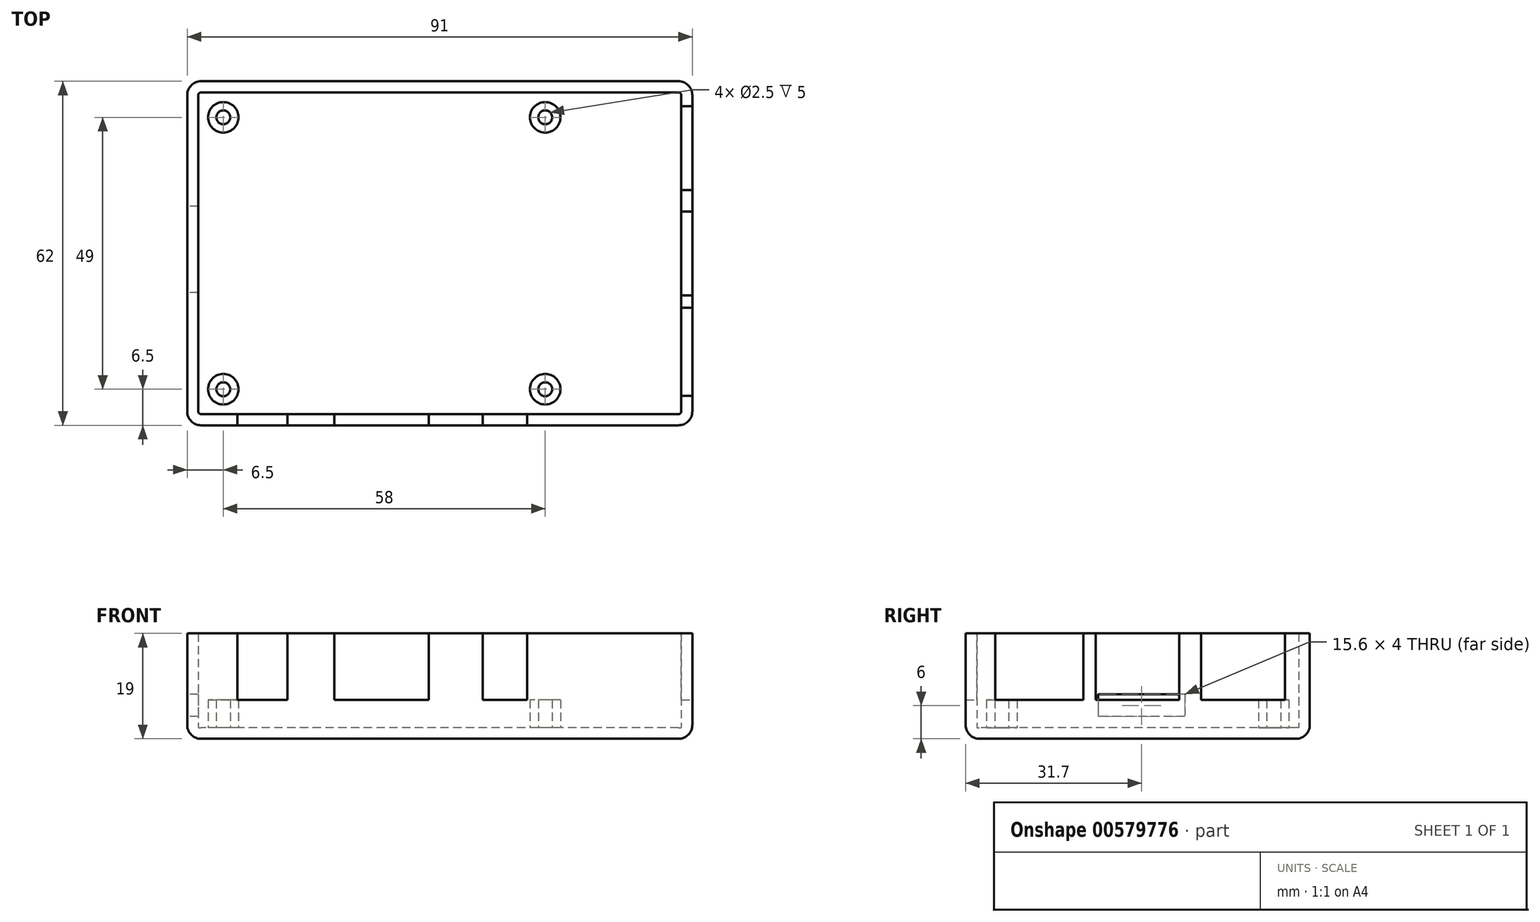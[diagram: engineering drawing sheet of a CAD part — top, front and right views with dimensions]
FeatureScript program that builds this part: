
annotation { "Feature Type Name" : "Feature", "Feature Type Description" : "" }
export const myFeature = defineFeature(function(context is Context, id is Id, definition is map)
    precondition{}
    {
        {
            var Q0;
            Q0=qCreatedBy(makeId("Top.planeOp"),FACE);
            var sketch = newSketch(context, id + "F0", { "sketchPlane" : qUnion([Q0])});
            skLineSegment(sketch, "E0.bottom", {"start": v(2.5, 0) * mm, "end": v(88.5, 0) * mm});
            skLineSegment(sketch, "E0.top", {"start": v(2.5, 62) * mm, "end": v(88.5, 62) * mm});
            skLineSegment(sketch, "E0.left", {"start": v(0, 2.5) * mm, "end": v(0, 59.5) * mm});
            skLineSegment(sketch, "E0.right", {"start": v(91, 2.5) * mm, "end": v(91, 59.5) * mm});
            skPoint(sketch, "E1.visualSharp", {"position": v(91, 62) * mm});
            skArc(sketch, "E1.filletArc", {"start": v(91, 59.5) * mm, "mid": v(90.27, 61.27) * mm, "end": v(88.5, 62) * mm});
            skPoint(sketch, "E2.visualSharp", {"position": v(91, 0) * mm});
            skArc(sketch, "E2.filletArc", {"start": v(88.5, 0) * mm, "mid": v(90.27, 0.73) * mm, "end": v(91, 2.5) * mm});
            skPoint(sketch, "E3.visualSharp", {"position": v(0, 0) * mm});
            skArc(sketch, "E3.filletArc", {"start": v(0, 2.5) * mm, "mid": v(0.73, 0.73) * mm, "end": v(2.5, 0) * mm});
            skPoint(sketch, "E4.visualSharp", {"position": v(0, 62) * mm});
            skArc(sketch, "E4.filletArc", {"start": v(2.5, 62) * mm, "mid": v(0.73, 61.27) * mm, "end": v(0, 59.5) * mm});
            skLineSegment(sketch, "E5.0", {"start": v(2.5, 60) * mm, "end": v(88.5, 60) * mm});
            skLineSegment(sketch, "E5.1", {"start": v(2, 2.5) * mm, "end": v(2, 59.5) * mm});
            skLineSegment(sketch, "E5.2", {"start": v(2.5, 2) * mm, "end": v(88.5, 2) * mm});
            skLineSegment(sketch, "E5.3", {"start": v(89, 2.5) * mm, "end": v(89, 59.5) * mm});
            skPoint(sketch, "E6.visualSharp", {"position": v(89, 60) * mm});
            skArc(sketch, "E6.filletArc", {"start": v(89, 59.5) * mm, "mid": v(88.85, 59.85) * mm, "end": v(88.5, 60) * mm});
            skPoint(sketch, "E7.visualSharp", {"position": v(89, 2) * mm});
            skArc(sketch, "E7.filletArc", {"start": v(88.5, 2) * mm, "mid": v(88.85, 2.15) * mm, "end": v(89, 2.5) * mm});
            skPoint(sketch, "E8.visualSharp", {"position": v(2, 2) * mm});
            skArc(sketch, "E8.filletArc", {"start": v(2, 2.5) * mm, "mid": v(2.15, 2.15) * mm, "end": v(2.5, 2) * mm});
            skPoint(sketch, "E9.visualSharp", {"position": v(2, 60) * mm});
            skArc(sketch, "E9.filletArc", {"start": v(2.5, 60) * mm, "mid": v(2.15, 59.85) * mm, "end": v(2, 59.5) * mm});
            skSolve(sketch);
        }
        {
            var Q0;
            Q0 = qSketchRegion(id + "F0", true);
            var Q1;
            Q1=makeQuery(id+"F0.imprint","IMPRINT",FACE,{"disambiguationData":[TD([[makeQuery(id+"F0.imprint","IMPRINT",EDGE,{"derivedFrom":sQuery(id+"F0.wireOp",EDGE,"E5.0")}),-1.0]])]});
            extrude(context, id + "F1", {"entities" : qUnion([Q0, Q1]), "depth" : 2 * mm, "offsetDistance" : 25 * mm});
        }
        {
            var Q0;
            Q0 = qSketchRegion(id + "F0", true);
            extrude(context, id + "F2", {"entities" : qUnion([Q0]), "operationType" : NewBodyOperationType.ADD, "depth" : 19 * mm, "offsetDistance" : 25 * mm});
        }
        {
            var Q0;
            Q0=makeQuery(id+"F1.opExtrude","CAP_FACE",FACE,{"disambiguationData":[OSD([sQuery(id+"F0.wireOp",EDGE,"E0.bottom"),sQuery(id+"F0.wireOp",EDGE,"E0.top"),sQuery(id+"F0.wireOp",EDGE,"E0.left"),sQuery(id+"F0.wireOp",EDGE,"E0.right"),sQuery(id+"F0.wireOp",EDGE,"E1.filletArc"),sQuery(id+"F0.wireOp",EDGE,"E2.filletArc"),sQuery(id+"F0.wireOp",EDGE,"E3.filletArc"),sQuery(id+"F0.wireOp",EDGE,"E4.filletArc")])],"isStart":false});
            var sketch = newSketch(context, id + "F3", { "sketchPlane" : qUnion([Q0])});
            skCircle(sketch, "E10", {"center": v(6.5, 55.5) * mm, "radius": 2.75 * mm});
            skCircle(sketch, "E11", {"center": v(64.5, 55.5) * mm, "radius": 2.75 * mm});
            skCircle(sketch, "E12", {"center": v(6.5, 6.5) * mm, "radius": 2.75 * mm});
            skCircle(sketch, "E13", {"center": v(64.5, 6.5) * mm, "radius": 2.75 * mm});
            skCircle(sketch, "E14", {"center": v(6.5, 55.5) * mm, "radius": 1.25 * mm});
            skCircle(sketch, "E15", {"center": v(64.5, 55.5) * mm, "radius": 1.25 * mm});
            skCircle(sketch, "E16", {"center": v(64.5, 6.5) * mm, "radius": 1.25 * mm});
            skCircle(sketch, "E17", {"center": v(6.5, 6.5) * mm, "radius": 1.25 * mm});
            skSolve(sketch);
        }
        {
            var Q0;
            Q0 = qSketchRegion(id + "F3", true);
            extrude(context, id + "F4", {"entities" : qUnion([Q0]), "operationType" : NewBodyOperationType.ADD, "depth" : 5 * mm, "offsetDistance" : 25 * mm});
        }
        {
            var Q0;
            Q0=makeQuery(id+"F2.opExtrude","CAP_FACE",FACE,{"disambiguationData":[OSD([sQuery(id+"F0.wireOp",EDGE,"E0.bottom"),sQuery(id+"F0.wireOp",EDGE,"E0.top"),sQuery(id+"F0.wireOp",EDGE,"E0.left"),sQuery(id+"F0.wireOp",EDGE,"E0.right"),sQuery(id+"F0.wireOp",EDGE,"E1.filletArc"),sQuery(id+"F0.wireOp",EDGE,"E2.filletArc"),sQuery(id+"F0.wireOp",EDGE,"E3.filletArc"),sQuery(id+"F0.wireOp",EDGE,"E4.filletArc"),sQuery(id+"F0.wireOp",EDGE,"E5.0"),sQuery(id+"F0.wireOp",EDGE,"E5.1"),sQuery(id+"F0.wireOp",EDGE,"E5.2"),sQuery(id+"F0.wireOp",EDGE,"E5.3"),sQuery(id+"F0.wireOp",EDGE,"E6.filletArc"),sQuery(id+"F0.wireOp",EDGE,"E7.filletArc"),sQuery(id+"F0.wireOp",EDGE,"E8.filletArc"),sQuery(id+"F0.wireOp",EDGE,"E9.filletArc")])],"isStart":false});
            var sketch = newSketch(context, id + "F5", { "sketchPlane" : qUnion([Q0])});
            skLineSegment(sketch, "E18.bottom", {"start": v(9.05, 0) * mm, "end": v(18.05, 0) * mm});
            skLineSegment(sketch, "E18.top", {"start": v(9.05, 2) * mm, "end": v(18.05, 2) * mm});
            skLineSegment(sketch, "E18.left", {"start": v(9.05, 0) * mm, "end": v(9.05, 2) * mm});
            skLineSegment(sketch, "E18.right", {"start": v(18.05, 0) * mm, "end": v(18.05, 2) * mm});
            skLineSegment(sketch, "E19.bottom", {"start": v(26.5, 0) * mm, "end": v(43.5, 0) * mm});
            skLineSegment(sketch, "E19.top", {"start": v(26.5, 2) * mm, "end": v(43.5, 2) * mm});
            skLineSegment(sketch, "E19.left", {"start": v(26.5, 0) * mm, "end": v(26.5, 2) * mm});
            skLineSegment(sketch, "E19.right", {"start": v(43.5, 0) * mm, "end": v(43.5, 2) * mm});
            skLineSegment(sketch, "E20.bottom", {"start": v(53.25, 0) * mm, "end": v(61.25, 0) * mm});
            skLineSegment(sketch, "E20.top", {"start": v(53.25, 2) * mm, "end": v(61.25, 2) * mm});
            skLineSegment(sketch, "E20.left", {"start": v(53.25, 0) * mm, "end": v(53.25, 2) * mm});
            skLineSegment(sketch, "E20.right", {"start": v(61.25, 0) * mm, "end": v(61.25, 2) * mm});
            skLineSegment(sketch, "E21.bottom", {"start": v(89, 57.5) * mm, "end": v(91, 57.5) * mm});
            skLineSegment(sketch, "E21.top", {"start": v(89, 42.4) * mm, "end": v(91, 42.4) * mm});
            skLineSegment(sketch, "E21.left", {"start": v(89, 57.5) * mm, "end": v(89, 42.4) * mm});
            skLineSegment(sketch, "E21.right", {"start": v(91, 57.5) * mm, "end": v(91, 42.4) * mm});
            skLineSegment(sketch, "E22.bottom", {"start": v(91, 38.5) * mm, "end": v(89, 38.5) * mm});
            skLineSegment(sketch, "E22.top", {"start": v(91, 23.4) * mm, "end": v(89, 23.4) * mm});
            skLineSegment(sketch, "E22.left", {"start": v(91, 38.5) * mm, "end": v(91, 23.4) * mm});
            skLineSegment(sketch, "E22.right", {"start": v(89, 38.5) * mm, "end": v(89, 23.4) * mm});
            skLineSegment(sketch, "E23.bottom", {"start": v(91, 21.2) * mm, "end": v(89, 21.2) * mm});
            skLineSegment(sketch, "E23.top", {"start": v(91, 5.3) * mm, "end": v(89, 5.3) * mm});
            skLineSegment(sketch, "E23.left", {"start": v(91, 21.2) * mm, "end": v(91, 5.3) * mm});
            skLineSegment(sketch, "E23.right", {"start": v(89, 21.2) * mm, "end": v(89, 5.3) * mm});
            skSolve(sketch);
        }
        {
            var Q0;
            Q0 = qSketchRegion(id + "F5", true);
            extrude(context, id + "F6", {"entities" : qUnion([Q0]), "operationType" : NewBodyOperationType.REMOVE, "oppositeDirection" : true, "depth" : 12 * mm, "offsetDistance" : 25 * mm});
        }
        {
            var Q0;
            {var subQ0=sQuery(id+"F0.wireOp",EDGE,"E0.left");Q0=makeQuery(id+"F2.boolean.opBoolean","MERGE",FACE,{"derivedFrom":[makeQuery(id+"F1.opExtrude","SWEPT_FACE",FACE,{"disambiguationData":[OSD([subQ0])]}),makeQuery(id+"F2.opExtrude","SWEPT_FACE",FACE,{"disambiguationData":[OSD([subQ0])]})]});}
            var sketch = newSketch(context, id + "F7", { "sketchPlane" : qUnion([Q0])});
            skLineSegment(sketch, "E24.bottom", {"start": v(-39.5, 8) * mm, "end": v(-23.9, 8) * mm});
            skLineSegment(sketch, "E24.top", {"start": v(-39.5, 4) * mm, "end": v(-23.9, 4) * mm});
            skLineSegment(sketch, "E24.left", {"start": v(-39.5, 8) * mm, "end": v(-39.5, 4) * mm});
            skLineSegment(sketch, "E24.right", {"start": v(-23.9, 8) * mm, "end": v(-23.9, 4) * mm});
            skSolve(sketch);
        }
        {
            var Q0;
            Q0 = qSketchRegion(id + "F7", true);
            extrude(context, id + "F8", {"entities" : qUnion([Q0]), "operationType" : NewBodyOperationType.REMOVE, "oppositeDirection" : true, "depth" : 5 * mm, "offsetDistance" : 25 * mm});
        }
        {
            var Q0;
            Q0=makeQuery(id+"F1.opExtrude","CAP_EDGE",EDGE,{"disambiguationData":[OSD([sQuery(id+"F0.wireOp",EDGE,"E0.bottom")])],"isStart":true});
            fillet(context, id + "F9", {"entities" : qUnion([Q0]), "radius" : 2.5 * mm, "tangentPropagation" : true, "allowEdgeOverflow" : false});
        }
    });
